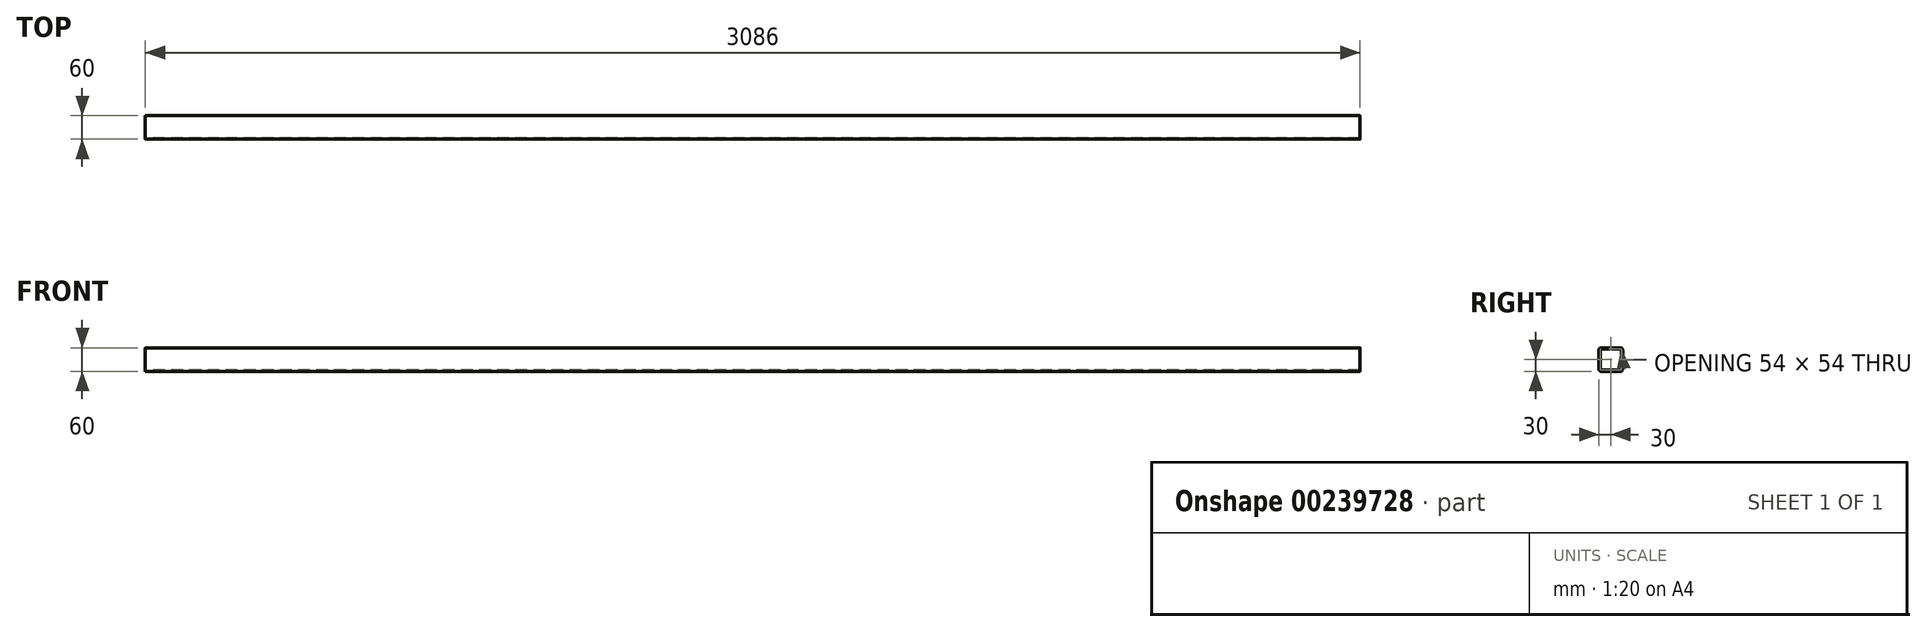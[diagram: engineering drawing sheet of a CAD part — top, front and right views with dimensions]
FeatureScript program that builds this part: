
annotation { "Feature Type Name" : "Feature", "Feature Type Description" : "" }
export const myFeature = defineFeature(function(context is Context, id is Id, definition is map)
    precondition{}
    {
        {
            var Q0;
            Q0=qCreatedBy(makeId("Right.planeOp"),FACE);
            var sketch = newSketch(context, id + "F0", { "sketchPlane" : qUnion([Q0])});
            skLineSegment(sketch, "E0.bottom", {"start": v(25, -30) * mm, "end": v(-25, -30) * mm});
            skLineSegment(sketch, "E0.top", {"start": v(25, 30) * mm, "end": v(-25, 30) * mm});
            skLineSegment(sketch, "E0.left", {"start": v(30, -25) * mm, "end": v(30, 25) * mm});
            skLineSegment(sketch, "E0.right", {"start": v(-30, -25) * mm, "end": v(-30, 25) * mm});
            skPoint(sketch, "E0.middle", {"position": v(0, 0) * mm});
            skPoint(sketch, "E1.visualSharp", {"position": v(-30, 30) * mm});
            skArc(sketch, "E1.filletArc", {"start": v(-25, 30) * mm, "mid": v(-28.54, 28.54) * mm, "end": v(-30, 25) * mm});
            skPoint(sketch, "E2.visualSharp", {"position": v(30, 30) * mm});
            skArc(sketch, "E2.filletArc", {"start": v(30, 25) * mm, "mid": v(28.54, 28.54) * mm, "end": v(25, 30) * mm});
            skPoint(sketch, "E3.visualSharp", {"position": v(30, -30) * mm});
            skArc(sketch, "E3.filletArc", {"start": v(25, -30) * mm, "mid": v(28.54, -28.54) * mm, "end": v(30, -25) * mm});
            skPoint(sketch, "E4.visualSharp", {"position": v(-30, -30) * mm});
            skArc(sketch, "E4.filletArc", {"start": v(-30, -25) * mm, "mid": v(-28.54, -28.54) * mm, "end": v(-25, -30) * mm});
            skLineSegment(sketch, "E5.0", {"start": v(25, 27) * mm, "end": v(-25, 27) * mm});
            skArc(sketch, "E5.1", {"start": v(27, 25) * mm, "mid": v(26.41, 26.41) * mm, "end": v(25, 27) * mm});
            skArc(sketch, "E5.2", {"start": v(-25, 27) * mm, "mid": v(-26.41, 26.41) * mm, "end": v(-27, 25) * mm});
            skLineSegment(sketch, "E5.3", {"start": v(27, -25) * mm, "end": v(27, 25) * mm});
            skLineSegment(sketch, "E5.4", {"start": v(-27, -25) * mm, "end": v(-27, 25) * mm});
            skArc(sketch, "E5.5", {"start": v(-27, -25) * mm, "mid": v(-26.41, -26.41) * mm, "end": v(-25, -27) * mm});
            skLineSegment(sketch, "E5.6", {"start": v(25, -27) * mm, "end": v(-25, -27) * mm});
            skArc(sketch, "E5.7", {"start": v(25, -27) * mm, "mid": v(26.41, -26.41) * mm, "end": v(27, -25) * mm});
            skSolve(sketch);
        }
        {
            var Q0;
            Q0=makeQuery(id+"F0.imprint","IMPRINT",FACE,{"disambiguationData":[TD([[makeQuery(id+"F0.imprint","IMPRINT",EDGE,{"derivedFrom":sQuery(id+"F0.wireOp",EDGE,"E0.bottom")}),-1.0]])]});
            extrude(context, id + "F1", {"entities" : qUnion([Q0]), "depth" : 3086 * mm});
        }
    });
